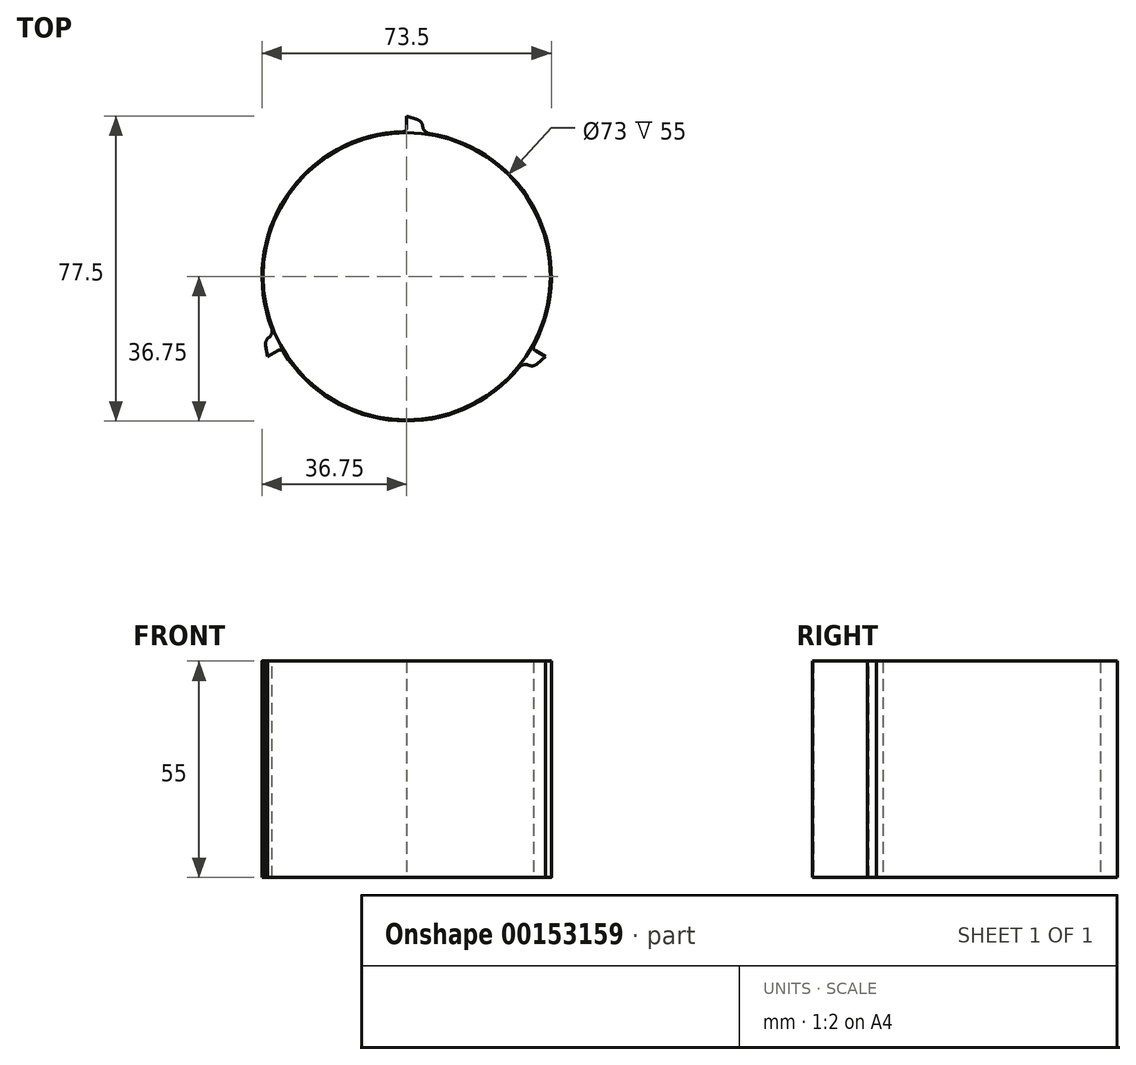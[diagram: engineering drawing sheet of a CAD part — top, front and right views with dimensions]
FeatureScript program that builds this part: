
annotation { "Feature Type Name" : "Feature", "Feature Type Description" : "" }
export const myFeature = defineFeature(function(context is Context, id is Id, definition is map)
    precondition{}
    {
        {
            var Q0;
            Q0=qCreatedBy(makeId("Top.planeOp"),FACE);
            var sketch = newSketch(context, id + "F0", { "sketchPlane" : qUnion([Q0])});
            skCircle(sketch, "E0", {"center": v(0, 0) * mm, "radius": 36.75 * mm});
            skCircle(sketch, "E1", {"center": v(0, 0) * mm, "radius": 36.5 * mm});
            skLineSegment(sketch, "E2", {"start": v(0, 36.75) * mm, "end": v(0, 40.75) * mm});
            skLineSegment(sketch, "E3", {"start": v(0, 40.75) * mm, "end": v(4.08, 39.31) * mm});
            skLineSegment(sketch, "E4", {"start": v(4.08, 39.31) * mm, "end": v(4.08, 36.52) * mm});
            skLineSegment(sketch, "E5.1.0", {"start": v(-35.3, -20.37) * mm, "end": v(-36.08, -16.13) * mm});
            skLineSegment(sketch, "E5.1.1", {"start": v(-36.08, -16.13) * mm, "end": v(-33.67, -14.73) * mm});
            skLineSegment(sketch, "E5.1.2", {"start": v(-31.83, -18.37) * mm, "end": v(-35.3, -20.37) * mm});
            skLineSegment(sketch, "E5.2.0", {"start": v(35.3, -20.37) * mm, "end": v(32, -23.19) * mm});
            skLineSegment(sketch, "E5.2.1", {"start": v(32, -23.19) * mm, "end": v(29.6, -21.8) * mm});
            skLineSegment(sketch, "E5.2.2", {"start": v(31.83, -18.38) * mm, "end": v(35.3, -20.38) * mm});
            skSolve(sketch);
        }
        {
            var Q0;
            Q0=makeQuery(id+"F0.imprint","IMPRINT",FACE,{"disambiguationData":[TD([[makeQuery(id+"F0.imprint","IMPRINT",EDGE,{"derivedFrom":sQuery(id+"F0.wireOp",EDGE,"E1")}),-1.0]])]});
            var Q1;
            {var subQ0=sQuery(id+"F0.wireOp",EDGE,"E2");Q1=makeQuery(id+"F0.imprint","IMPRINT",FACE,{"disambiguationData":[TD([[makeQuery(id+"F0.imprint","IMPRINT",EDGE,{"derivedFrom":subQ0}),-1.0]])]});}
            var Q2;
            Q2=makeQuery(id+"F0.imprint","IMPRINT",FACE,{"disambiguationData":[TD([[makeQuery(id+"F0.imprint","IMPRINT",EDGE,{"derivedFrom":sQuery(id+"F0.wireOp",EDGE,"E5.1.0")}),-1.0]])]});
            var Q3;
            Q3=makeQuery(id+"F0.imprint","IMPRINT",FACE,{"disambiguationData":[TD([[makeQuery(id+"F0.imprint","IMPRINT",EDGE,{"derivedFrom":sQuery(id+"F0.wireOp",EDGE,"E5.2.0")}),-1.0]])]});
            extrude(context, id + "F1", {"entities" : qUnion([Q0, Q1, Q2, Q3]), "depth" : 55 * mm});
        }
        {
            var Q0;
            Q0=makeQuery(id+"F1.opExtrude","SWEPT_EDGE",EDGE,{"disambiguationData":[OSD([sQuery(id+"F0.wireOp",EDGE,"E3"),sQuery(id+"F0.wireOp",EDGE,"E4")])]});
            fillet(context, id + "F2", {"entities" : qUnion([Q0]), "radius" : 2 * mm, "tangentPropagation" : true, "allowEdgeOverflow" : false});
        }
        {
            var Q0;
            Q0=makeQuery(id+"F1.opExtrude","SWEPT_EDGE",EDGE,{"disambiguationData":[OSD([sQuery(id+"F0.wireOp",EDGE,"E0"),sQuery(id+"F0.wireOp",EDGE,"E4")])]});
            fillet(context, id + "F3", {"entities" : qUnion([Q0]), "radius" : 2 * mm, "tangentPropagation" : true, "allowEdgeOverflow" : false});
        }
        {
            var Q0;
            Q0=makeQuery(id+"F1.opExtrude","SWEPT_EDGE",EDGE,{"disambiguationData":[OSD([sQuery(id+"F0.wireOp",EDGE,"E0"),sQuery(id+"F0.wireOp",EDGE,"E2")])]});
            fillet(context, id + "F4", {"entities" : qUnion([Q0]), "radius" : 1 * mm, "tangentPropagation" : true, "allowEdgeOverflow" : false});
        }
        {
            var Q0;
            Q0=makeQuery(id+"F1.opExtrude","SWEPT_EDGE",EDGE,{"disambiguationData":[OSD([sQuery(id+"F0.wireOp",EDGE,"E5.2.0"),sQuery(id+"F0.wireOp",EDGE,"E5.2.1")])]});
            fillet(context, id + "F5", {"entities" : qUnion([Q0]), "radius" : 2 * mm, "tangentPropagation" : true, "allowEdgeOverflow" : false});
        }
        {
            var Q0;
            Q0=makeQuery(id+"F1.opExtrude","SWEPT_EDGE",EDGE,{"disambiguationData":[OSD([sQuery(id+"F0.wireOp",EDGE,"E0"),sQuery(id+"F0.wireOp",EDGE,"E5.2.1")])]});
            fillet(context, id + "F6", {"entities" : qUnion([Q0]), "radius" : 2 * mm, "tangentPropagation" : true, "allowEdgeOverflow" : false});
        }
        {
            var Q0;
            Q0=makeQuery(id+"F1.opExtrude","SWEPT_EDGE",EDGE,{"disambiguationData":[OSD([sQuery(id+"F0.wireOp",EDGE,"E0"),sQuery(id+"F0.wireOp",EDGE,"E5.2.2")])]});
            fillet(context, id + "F7", {"entities" : qUnion([Q0]), "radius" : 1 * mm, "tangentPropagation" : true, "allowEdgeOverflow" : false});
        }
        {
            var Q0;
            Q0=makeQuery(id+"F1.opExtrude","SWEPT_EDGE",EDGE,{"disambiguationData":[OSD([sQuery(id+"F0.wireOp",EDGE,"E0"),sQuery(id+"F0.wireOp",EDGE,"E5.1.2")])]});
            fillet(context, id + "F8", {"entities" : qUnion([Q0]), "radius" : 1 * mm, "tangentPropagation" : true, "allowEdgeOverflow" : false});
        }
        {
            var Q0;
            Q0=makeQuery(id+"F1.opExtrude","SWEPT_EDGE",EDGE,{"disambiguationData":[OSD([sQuery(id+"F0.wireOp",EDGE,"E5.1.0"),sQuery(id+"F0.wireOp",EDGE,"E5.1.1")])]});
            fillet(context, id + "F9", {"entities" : qUnion([Q0]), "radius" : 2 * mm, "tangentPropagation" : true, "allowEdgeOverflow" : false});
        }
        {
            var Q0;
            Q0=makeQuery(id+"F1.opExtrude","SWEPT_EDGE",EDGE,{"disambiguationData":[OSD([sQuery(id+"F0.wireOp",EDGE,"E0"),sQuery(id+"F0.wireOp",EDGE,"E5.1.1")])]});
            fillet(context, id + "F10", {"entities" : qUnion([Q0]), "radius" : 2 * mm, "tangentPropagation" : true, "allowEdgeOverflow" : false});
        }
    });
